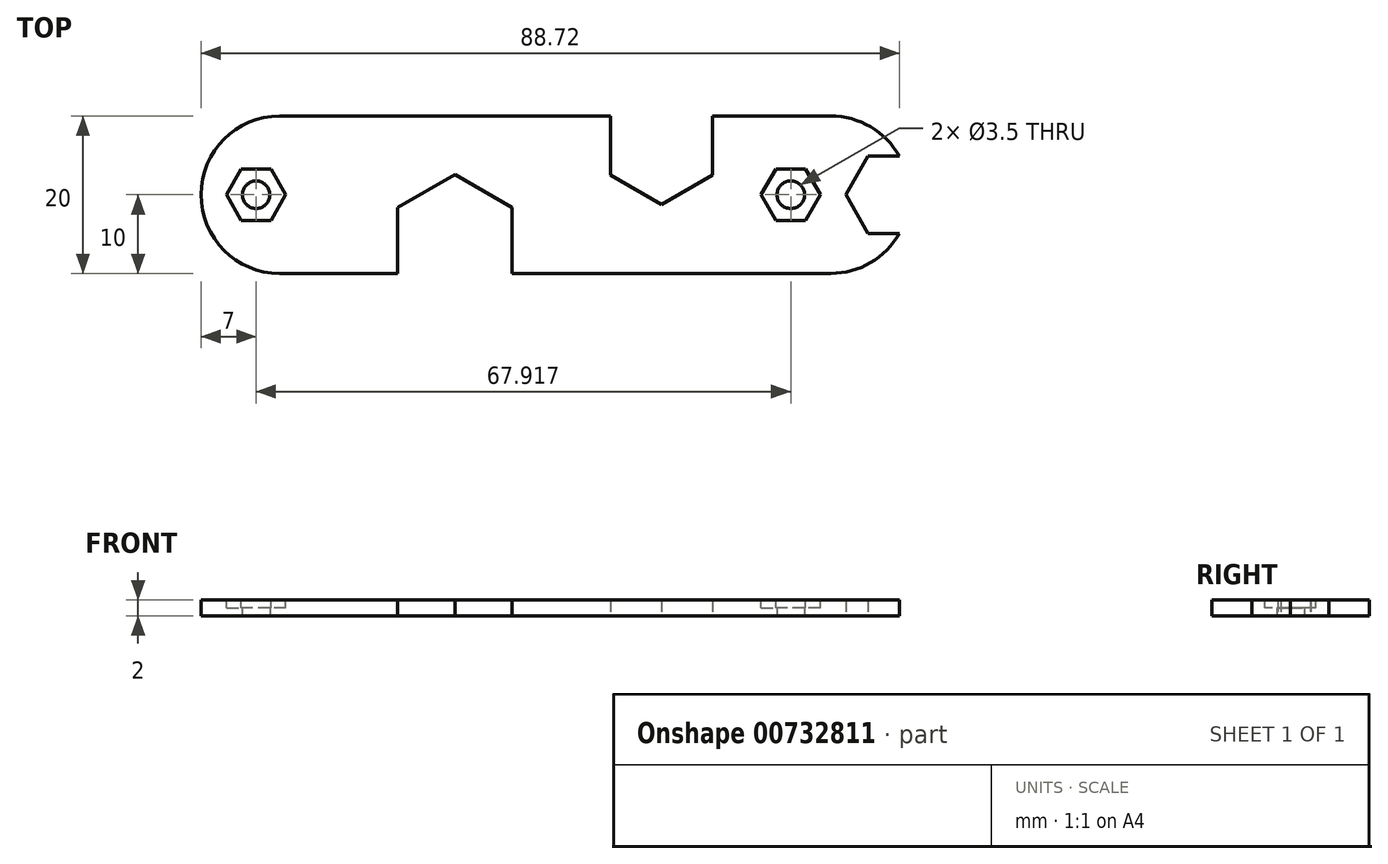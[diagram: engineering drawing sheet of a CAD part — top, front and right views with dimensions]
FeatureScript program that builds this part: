
annotation { "Feature Type Name" : "Feature", "Feature Type Description" : "" }
export const myFeature = defineFeature(function(context is Context, id is Id, definition is map)
    precondition{}
    {
        {
            var Q0;
            Q0=qCreatedBy(makeId("Top.planeOp"),FACE);
            var sketch = newSketch(context, id + "F0", { "sketchPlane" : qUnion([Q0])});
            skArc(sketch, "E0", {"start": v(36.44, 10) * mm, "mid": v(26.44, 0) * mm, "end": v(36.44, -10) * mm});
            skArc(sketch, "E1", {"start": v(106.44, -10) * mm, "mid": v(111.57, -8.59) * mm, "end": v(115.24, -4.74) * mm});
            skLineSegment(sketch, "E2", {"start": v(36.44, -10) * mm, "end": v(51.44, -10) * mm});
            skLineSegment(sketch, "E3", {"start": v(106.44, 10) * mm, "end": v(91.44, 10) * mm});
            skCircle(sketch, "E4.cCircle", {"center": v(58.69, -5.81) * mm, "radius": 7.25 * mm, "construction": true});
            skLineSegment(sketch, "E4.0", {"start": v(51.44, -10) * mm, "end": v(51.44, -1.63) * mm});
            skLineSegment(sketch, "E4.1", {"start": v(51.44, -1.63) * mm, "end": v(58.69, 2.56) * mm});
            skLineSegment(sketch, "E4.2", {"start": v(58.69, 2.56) * mm, "end": v(65.94, -1.63) * mm});
            skLineSegment(sketch, "E4.3", {"start": v(65.94, -1.63) * mm, "end": v(65.94, -10) * mm});
            skPoint(sketch, "E4.0.midPoint", {"position": v(51.44, -5.81) * mm});
            skCircle(sketch, "E5.cCircle", {"center": v(84.94, 6.25) * mm, "radius": 6.5 * mm, "construction": true});
            skLineSegment(sketch, "E5.0", {"start": v(78.44, 2.5) * mm, "end": v(78.44, 10) * mm});
            skLineSegment(sketch, "E5.3", {"start": v(91.44, 10) * mm, "end": v(91.44, 2.5) * mm});
            skLineSegment(sketch, "E5.4", {"start": v(91.44, 2.5) * mm, "end": v(84.94, -1.26) * mm});
            skLineSegment(sketch, "E5.5", {"start": v(84.94, -1.26) * mm, "end": v(78.44, 2.5) * mm});
            skPoint(sketch, "E5.0.midPoint", {"position": v(78.44, 6.25) * mm});
            skCircle(sketch, "E6.cCircle", {"center": v(114.01, 0) * mm, "radius": 4.9 * mm, "construction": true});
            skLineSegment(sketch, "E6.0", {"start": v(115.16, -4.9) * mm, "end": v(111.19, -4.9) * mm});
            skLineSegment(sketch, "E6.1", {"start": v(111.19, -4.9) * mm, "end": v(108.36, 0) * mm});
            skLineSegment(sketch, "E6.2", {"start": v(108.36, 0) * mm, "end": v(111.19, 4.9) * mm});
            skLineSegment(sketch, "E6.3", {"start": v(111.19, 4.9) * mm, "end": v(115.16, 4.9) * mm});
            skPoint(sketch, "E6.0.midPoint", {"position": v(114.01, -4.9) * mm});
            skCircle(sketch, "E7", {"center": v(33.44, 0) * mm, "radius": 1.75 * mm});
            skCircle(sketch, "E8", {"center": v(101.36, 0) * mm, "radius": 1.75 * mm});
            skArc(sketch, "E9.trimOffspring", {"start": v(115.24, 4.74) * mm, "mid": v(111.57, 8.59) * mm, "end": v(106.44, 10) * mm});
            skPoint(sketch, "E10.orphan", {"position": v(116.84, 4.9) * mm});
            skPoint(sketch, "E6.5.end.orphan", {"position": v(116.84, -4.9) * mm});
            skLineSegment(sketch, "E11.trimOffspring", {"start": v(78.44, 10) * mm, "end": v(36.44, 10) * mm});
            skPoint(sketch, "E12.orphan", {"position": v(84.94, 13.75) * mm});
            skLineSegment(sketch, "E13.trimOffspring", {"start": v(65.94, -10) * mm, "end": v(106.44, -10) * mm});
            skSolve(sketch);
        }
        {
            var Q0;
            Q0 = qSketchRegion(id + "F0", true);
            extrude(context, id + "F1", {"entities" : qUnion([Q0]), "depth" : 2 * mm, "offsetDistance" : 25 * mm});
        }
        {
            var Q0;
            Q0=makeQuery(id+"F1.opExtrude","CAP_FACE",FACE,{"disambiguationData":[OSD([sQuery(id+"F0.wireOp",EDGE,"E0"),sQuery(id+"F0.wireOp",EDGE,"E1"),sQuery(id+"F0.wireOp",EDGE,"E2"),sQuery(id+"F0.wireOp",EDGE,"E3"),sQuery(id+"F0.wireOp",EDGE,"E4.0"),sQuery(id+"F0.wireOp",EDGE,"E4.1"),sQuery(id+"F0.wireOp",EDGE,"E4.2"),sQuery(id+"F0.wireOp",EDGE,"E4.3"),sQuery(id+"F0.wireOp",EDGE,"E5.0"),sQuery(id+"F0.wireOp",EDGE,"E5.3"),sQuery(id+"F0.wireOp",EDGE,"E5.4"),sQuery(id+"F0.wireOp",EDGE,"E5.5"),sQuery(id+"F0.wireOp",EDGE,"E6.0"),sQuery(id+"F0.wireOp",EDGE,"E6.1"),sQuery(id+"F0.wireOp",EDGE,"E6.2"),sQuery(id+"F0.wireOp",EDGE,"E6.3"),sQuery(id+"F0.wireOp",EDGE,"E7"),sQuery(id+"F0.wireOp",EDGE,"E8"),sQuery(id+"F0.wireOp",EDGE,"E9.trimOffspring"),sQuery(id+"F0.wireOp",EDGE,"E11.trimOffspring"),sQuery(id+"F0.wireOp",EDGE,"E13.trimOffspring")])],"isStart":false});
            var sketch = newSketch(context, id + "F2", { "sketchPlane" : qUnion([Q0])});
            skCircle(sketch, "E14.cCircle", {"center": v(33.44, 0) * mm, "radius": 3.25 * mm, "construction": true});
            skLineSegment(sketch, "E14.0", {"start": v(35.32, -3.25) * mm, "end": v(31.56, -3.25) * mm});
            skLineSegment(sketch, "E14.1", {"start": v(31.56, -3.25) * mm, "end": v(29.69, 0) * mm});
            skLineSegment(sketch, "E14.2", {"start": v(29.69, 0) * mm, "end": v(31.56, 3.25) * mm});
            skLineSegment(sketch, "E14.3", {"start": v(31.56, 3.25) * mm, "end": v(35.32, 3.25) * mm});
            skLineSegment(sketch, "E14.4", {"start": v(35.32, 3.25) * mm, "end": v(37.2, 0) * mm});
            skLineSegment(sketch, "E14.5", {"start": v(37.2, 0) * mm, "end": v(35.32, -3.25) * mm});
            skPoint(sketch, "E14.0.midPoint", {"position": v(33.44, -3.25) * mm});
            skCircle(sketch, "E15.cCircle", {"center": v(101.36, 0) * mm, "radius": 3.25 * mm, "construction": true});
            skLineSegment(sketch, "E15.0", {"start": v(103.23, -3.25) * mm, "end": v(99.48, -3.25) * mm});
            skLineSegment(sketch, "E15.1", {"start": v(99.48, -3.25) * mm, "end": v(97.6, 0) * mm});
            skLineSegment(sketch, "E15.2", {"start": v(97.6, 0) * mm, "end": v(99.48, 3.25) * mm});
            skLineSegment(sketch, "E15.3", {"start": v(99.48, 3.25) * mm, "end": v(103.23, 3.25) * mm});
            skLineSegment(sketch, "E15.4", {"start": v(103.23, 3.25) * mm, "end": v(105.1, 0) * mm});
            skLineSegment(sketch, "E15.5", {"start": v(105.1, 0) * mm, "end": v(103.23, -3.25) * mm});
            skPoint(sketch, "E15.0.midPoint", {"position": v(101.36, -3.25) * mm});
            skSolve(sketch);
        }
        {
            var Q0;
            Q0 = qSketchRegion(id + "F2", true);
            extrude(context, id + "F3", {"entities" : qUnion([Q0]), "operationType" : NewBodyOperationType.REMOVE, "oppositeDirection" : true, "depth" : 1 * mm, "offsetDistance" : 25 * mm});
        }
    });
